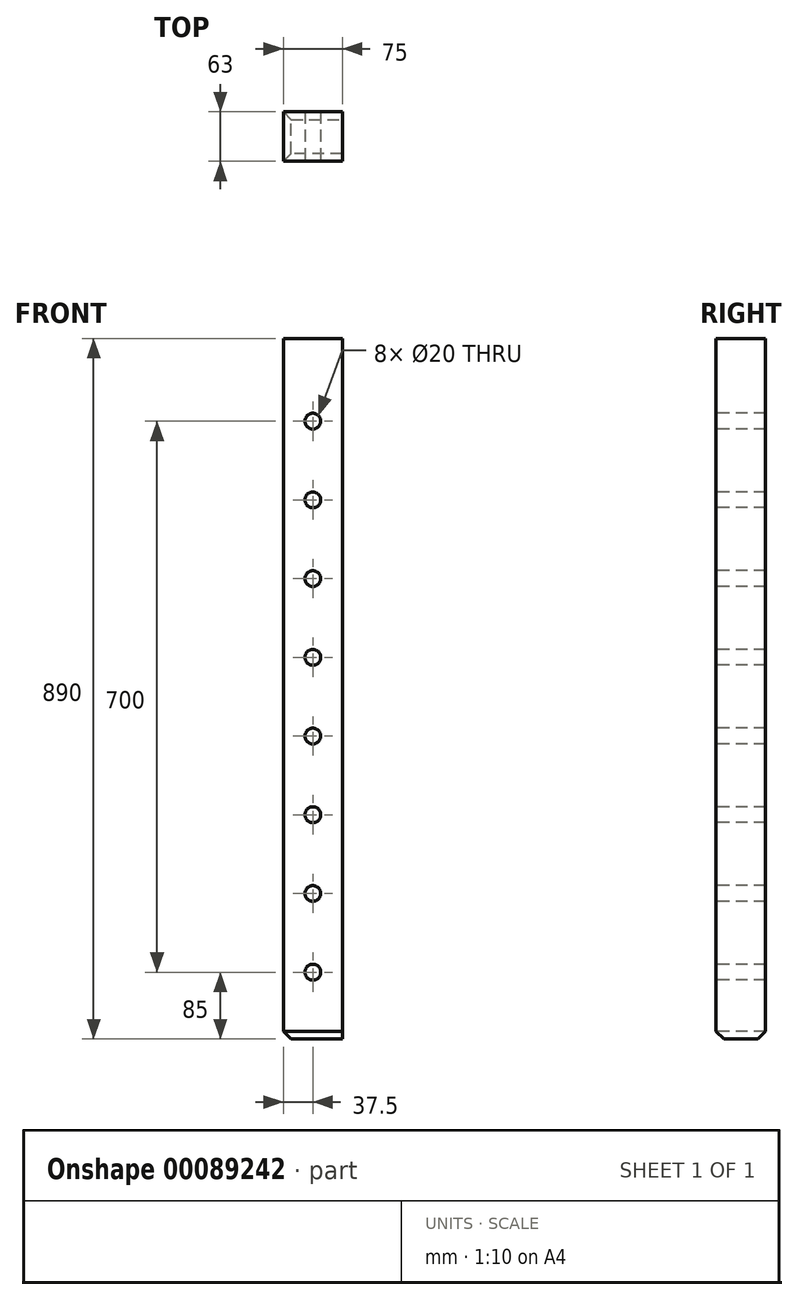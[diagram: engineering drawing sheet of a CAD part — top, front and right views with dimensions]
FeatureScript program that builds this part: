
annotation { "Feature Type Name" : "Feature", "Feature Type Description" : "" }
export const myFeature = defineFeature(function(context is Context, id is Id, definition is map)
    precondition{}
    {
        {
            var Q0;
            Q0=qCreatedBy(makeId("Top.planeOp"),FACE);
            var sketch = newSketch(context, id + "F0", { "sketchPlane" : qUnion([Q0])});
            skLineSegment(sketch, "E0.bottom", {"start": v(-37.5, 32.8) * mm, "end": v(37.5, 32.8) * mm});
            skLineSegment(sketch, "E0.top", {"start": v(-37.5, -30.2) * mm, "end": v(37.5, -30.2) * mm});
            skLineSegment(sketch, "E0.left", {"start": v(-37.5, 32.8) * mm, "end": v(-37.5, -30.2) * mm});
            skLineSegment(sketch, "E0.right", {"start": v(37.5, 32.8) * mm, "end": v(37.5, -30.2) * mm});
            skPoint(sketch, "E0.middle", {"position": v(0, 1.3) * mm});
            skSolve(sketch);
        }
        {
            var Q0;
            Q0=makeQuery(id+"F0.imprint","IMPRINT",FACE,{"disambiguationData":[TD([[makeQuery(id+"F0.imprint","IMPRINT",EDGE,{"derivedFrom":sQuery(id+"F0.wireOp",EDGE,"E0.bottom")}),-1.0]])]});
            extrude(context, id + "F1", {"entities" : qUnion([Q0]), "depth" : 890 * mm});
        }
        {
            var Q0;
            Q0=makeQuery(id+"F1.opExtrude","SWEPT_FACE",FACE,{"disambiguationData":[OSD([sQuery(id+"F0.wireOp",EDGE,"E0.top")])]});
            var sketch = newSketch(context, id + "F2", { "sketchPlane" : qUnion([Q0])});
            skLineSegment(sketch, "E1", {"start": v(0, 0) * mm, "end": v(0, 890) * mm, "construction": true});
            skCircle(sketch, "E2", {"center": v(0, 85) * mm, "radius": 10 * mm});
            skCircle(sketch, "E3.0.1.0", {"center": v(0, 185) * mm, "radius": 10 * mm});
            skCircle(sketch, "E3.0.2.0", {"center": v(0, 285) * mm, "radius": 10 * mm});
            skCircle(sketch, "E3.0.3.0", {"center": v(0, 385) * mm, "radius": 10 * mm});
            skCircle(sketch, "E3.0.4.0", {"center": v(0, 485) * mm, "radius": 10 * mm});
            skCircle(sketch, "E3.0.5.0", {"center": v(0, 585) * mm, "radius": 10 * mm});
            skCircle(sketch, "E3.0.6.0", {"center": v(0, 685) * mm, "radius": 10 * mm});
            skCircle(sketch, "E3.0.7.0", {"center": v(0, 785) * mm, "radius": 10 * mm});
            skLineSegment(sketch, "E3.direction1", {"start": v(0, 85) * mm, "end": v(25, 85) * mm, "construction": true});
            skLineSegment(sketch, "E3.direction2", {"start": v(0, 85) * mm, "end": v(0, 185) * mm, "construction": true});
            skSolve(sketch);
        }
        {
            var Q0;
            Q0=makeQuery(id+"F2.imprint","IMPRINT",FACE,{"disambiguationData":[TD([[makeQuery(id+"F2.imprint","IMPRINT",EDGE,{"derivedFrom":sQuery(id+"F2.wireOp",EDGE,"E2")}),1.0]])]});
            var Q1;
            Q1=makeQuery(id+"F2.imprint","IMPRINT",FACE,{"disambiguationData":[TD([[makeQuery(id+"F2.imprint","IMPRINT",EDGE,{"derivedFrom":sQuery(id+"F2.wireOp",EDGE,"E3.0.1.0")}),1.0]])]});
            var Q2;
            Q2=makeQuery(id+"F2.imprint","IMPRINT",FACE,{"disambiguationData":[TD([[makeQuery(id+"F2.imprint","IMPRINT",EDGE,{"derivedFrom":sQuery(id+"F2.wireOp",EDGE,"E3.0.2.0")}),1.0]])]});
            var Q3;
            Q3=makeQuery(id+"F2.imprint","IMPRINT",FACE,{"disambiguationData":[TD([[makeQuery(id+"F2.imprint","IMPRINT",EDGE,{"derivedFrom":sQuery(id+"F2.wireOp",EDGE,"E3.0.3.0")}),1.0]])]});
            var Q4;
            Q4=makeQuery(id+"F2.imprint","IMPRINT",FACE,{"disambiguationData":[TD([[makeQuery(id+"F2.imprint","IMPRINT",EDGE,{"derivedFrom":sQuery(id+"F2.wireOp",EDGE,"E3.0.4.0")}),1.0]])]});
            var Q5;
            Q5=makeQuery(id+"F2.imprint","IMPRINT",FACE,{"disambiguationData":[TD([[makeQuery(id+"F2.imprint","IMPRINT",EDGE,{"derivedFrom":sQuery(id+"F2.wireOp",EDGE,"E3.0.5.0")}),1.0]])]});
            var Q6;
            Q6=makeQuery(id+"F2.imprint","IMPRINT",FACE,{"disambiguationData":[TD([[makeQuery(id+"F2.imprint","IMPRINT",EDGE,{"derivedFrom":sQuery(id+"F2.wireOp",EDGE,"E3.0.6.0")}),1.0]])]});
            var Q7;
            Q7=makeQuery(id+"F2.imprint","IMPRINT",FACE,{"disambiguationData":[TD([[makeQuery(id+"F2.imprint","IMPRINT",EDGE,{"derivedFrom":sQuery(id+"F2.wireOp",EDGE,"E3.0.7.0")}),1.0]])]});
            extrude(context, id + "F3", {"entities" : qUnion([Q0, Q1, Q2, Q3, Q4, Q5, Q6, Q7]), "operationType" : NewBodyOperationType.REMOVE, "endBound" : BoundingType.THROUGH_ALL, "oppositeDirection" : true, "depth" : 25 * mm});
        }
        {
            var Q0;
            Q0=makeQuery(id+"F1.opExtrude","CAP_EDGE",EDGE,{"disambiguationData":[OSD([sQuery(id+"F0.wireOp",EDGE,"E0.bottom")])],"isStart":true});
            var Q1;
            Q1=makeQuery(id+"F1.opExtrude","CAP_EDGE",EDGE,{"disambiguationData":[OSD([sQuery(id+"F0.wireOp",EDGE,"E0.left")])],"isStart":true});
            var Q2;
            Q2=makeQuery(id+"F1.opExtrude","CAP_EDGE",EDGE,{"disambiguationData":[OSD([sQuery(id+"F0.wireOp",EDGE,"E0.top")])],"isStart":true});
            chamfer(context, id + "F4", {"entities" : qUnion([Q0, Q1, Q2]), "width" : 10 * mm, "tangentPropagation" : true});
        }
    });
